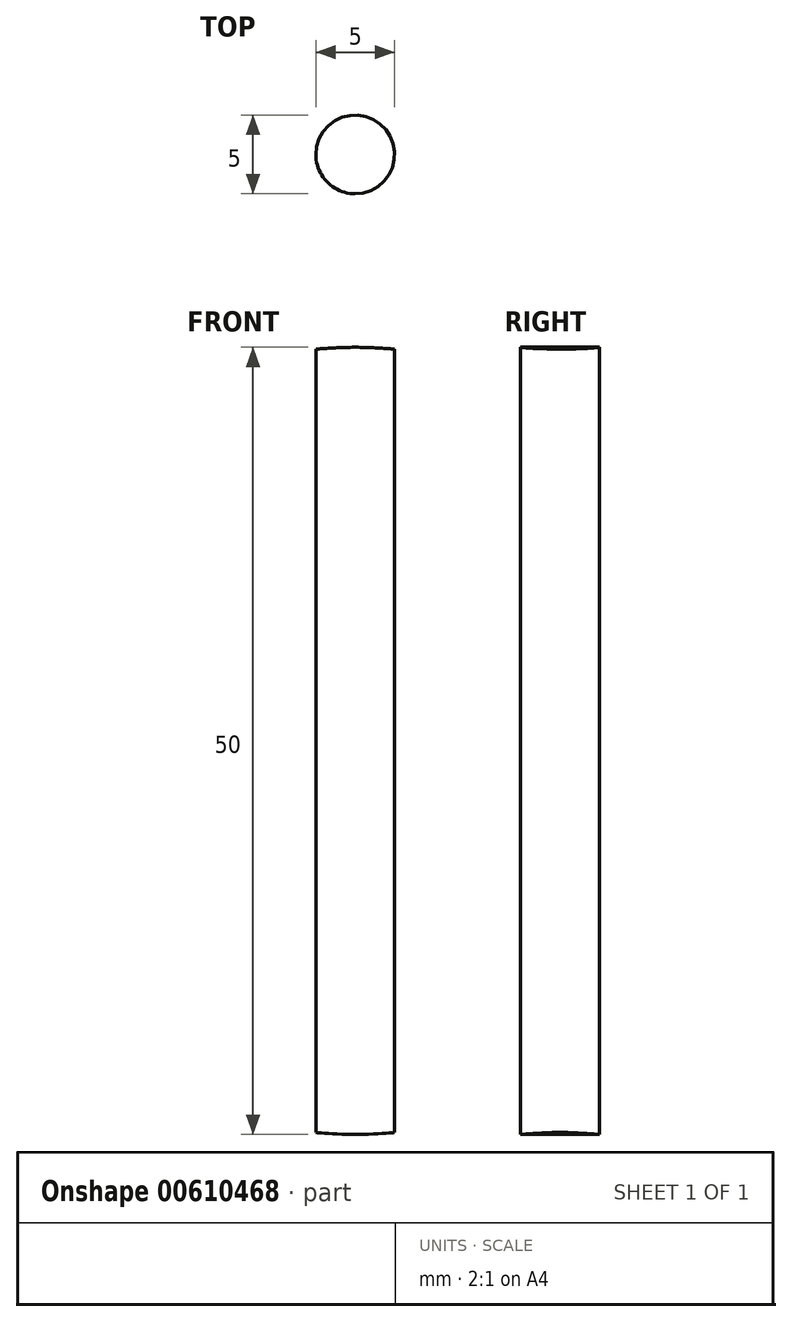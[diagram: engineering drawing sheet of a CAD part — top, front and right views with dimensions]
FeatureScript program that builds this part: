
annotation { "Feature Type Name" : "Feature", "Feature Type Description" : "" }
export const myFeature = defineFeature(function(context is Context, id is Id, definition is map)
    precondition{}
    {
        {
            var Q0;
            Q0=qCreatedBy(makeId("Top.planeOp"),FACE);
            var sketch = newSketch(context, id + "F0", { "sketchPlane" : qUnion([Q0])});
            skPoint(sketch, "E0.middle", {"position": v(0, 0) * mm});
            skCircle(sketch, "E1", {"center": v(0, 0) * mm, "radius": 2.5 * mm});
            skSolve(sketch);
        }
        {
            var Q0;
            Q0 = qSketchRegion(id + "F0", true);
            extrude(context, id + "F1", {"entities" : qUnion([Q0]), "depth" : 50 * mm, "offsetDistance" : 25 * mm});
        }
        {
            var Q0;
            Q0=qCreatedBy(makeId("Front.planeOp"),FACE);
            var sketch = newSketch(context, id + "F2", { "sketchPlane" : qUnion([Q0])});
            skCircle(sketch, "E2", {"center": v(0, 25) * mm, "radius": 25 * mm});
            skCircle(sketch, "E3", {"center": v(0, 25) * mm, "radius": 26.73 * mm});
            skSolve(sketch);
        }
        {
            var Q0;
            Q0=makeQuery(id+"F2.imprint","IMPRINT",FACE,{"disambiguationData":[TD([[makeQuery(id+"F2.imprint","IMPRINT",EDGE,{"derivedFrom":sQuery(id+"F2.wireOp",EDGE,"E2")}),-1.0]])]});
            extrude(context, id + "F3", {"entities" : qUnion([Q0]), "operationType" : NewBodyOperationType.REMOVE, "endBound" : BoundingType.SYMMETRIC, "oppositeDirection" : true, "depth" : 25 * mm, "offsetDistance" : 25 * mm});
        }
    });
